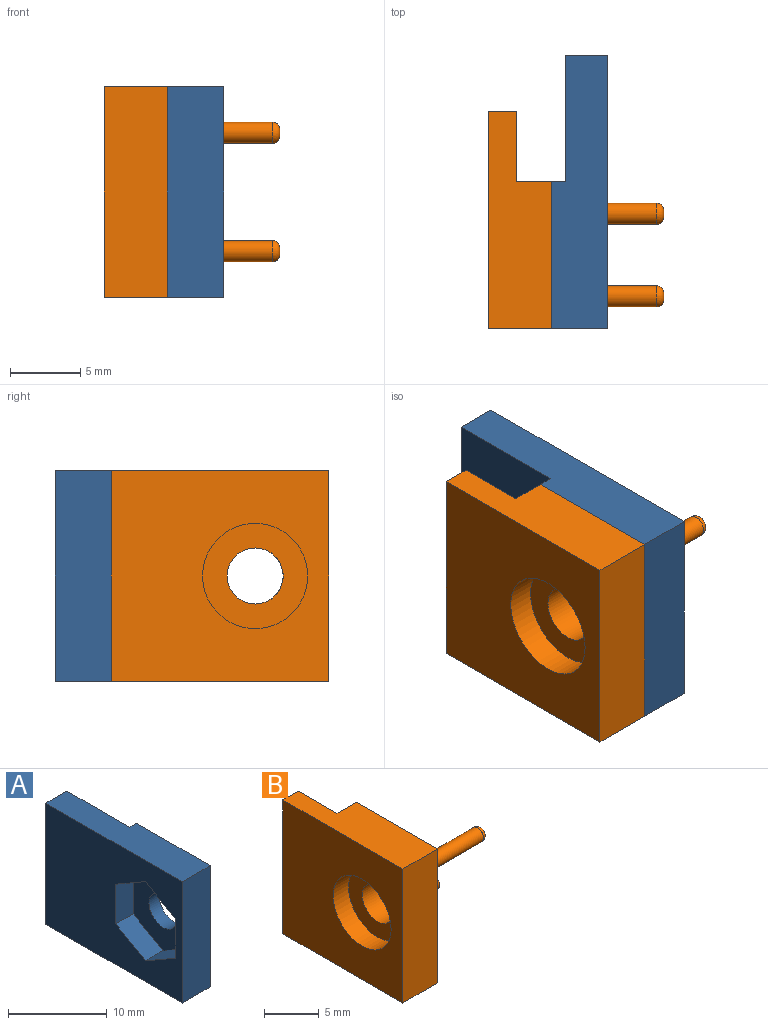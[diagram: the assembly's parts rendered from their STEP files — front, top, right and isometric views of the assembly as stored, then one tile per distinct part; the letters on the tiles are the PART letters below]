
ASSEMBLY  parts=2 mates=1
PART A: 16 faces, bbox 4x19.5x15 mm
  f0: cylinder r=2mm len=4mm, axis (1,0,0), area 18.8mm2, adj f4,f15
  f1: plane 15x3mm, normal (0,1,0), area 45mm2, adj f2,f6,f7,f8
  f2: plane 19.5x15mm, normal (-1,0,0), area 229.9mm2, adj f1,f3,f7,f8,f9,f10,f11,f12
  f3: plane 15x4mm, normal (0,-1,0), area 60mm2, adj f2,f4,f7,f8
  f4: plane 15x10.5mm, normal (1,0,0), area 144.9mm2, adj f0,f3,f5,f7,f8
  f5: plane 15x1mm, normal (0,1,0), area 15mm2, adj f4,f6,f7,f8
  f6: plane 15x9mm, normal (1,0,0), area 135mm2, adj f1,f5,f7,f8
  f7: plane 19.5x4mm, normal (0,0,1), area 69mm2, adj f1,f2,f3,f4,f5,f6
  f8: plane 19.5x4mm, normal (0,0,-1), area 69mm2, adj f1,f2,f3,f4,f5,f6
  f9: plane 4.25x2.5mm, normal (0,0.5,0.87), area 12.3mm2, adj f2,f10,f14,f15
  f10: plane 4.91x2.5mm, normal (0,1,0), area 12.3mm2, adj f2,f9,f11,f15
  f11: plane 4.25x2.5mm, normal (0,0.5,-0.87), area 12.3mm2, adj f2,f10,f12,f15
  f12: plane 4.25x2.5mm, normal (0,-0.5,-0.87), area 12.3mm2, adj f2,f11,f13,f15
  f13: plane 4.91x2.5mm, normal (0,-1,0), area 12.3mm2, adj f2,f12,f14,f15
  f14: plane 4.25x2.5mm, normal (0,-0.5,0.87), area 12.3mm2, adj f2,f9,f13,f15
  f15: plane 9.82x8.5mm, normal (-1,0,0), area 50mm2, adj f0,f9,f10,f11,f12,f13,f14
PART B: 17 faces, bbox 12.5x15.5x15 mm
  f0: cylinder r=2mm len=4mm, axis (1,0,0), area 31.4mm2, adj f4,f9
  f1: plane 15x2mm, normal (0,1,0), area 30mm2, adj f2,f6,f7,f8
  f2: plane 15.5x15mm, normal (-1,0,0), area 188.3mm2, adj f1,f3,f7,f8,f10
  f3: plane 15x4.5mm, normal (0,-1,0), area 67.5mm2, adj f2,f4,f7,f8
  f4: plane 15x10.5mm, normal (1,0,0), area 141.4mm2, adj f0,f3,f5,f7,f8,f11,f13
  f5: plane 15x2.5mm, normal (0,1,0), area 37.5mm2, adj f4,f6,f7,f8
  f6: plane 15x5mm, normal (1,0,0), area 75mm2, adj f1,f5,f7,f8
  f7: plane 15.5x4.5mm, normal (0,0,1), area 57.2mm2, adj f1,f2,f3,f4,f5,f6
  f8: plane 15.5x4.5mm, normal (0,0,-1), area 57.2mm2, adj f1,f2,f3,f4,f5,f6
  f9: plane 7.5x7.5mm, normal (-1,0,0), area 31.6mm2, adj f0,f10
  f10: cylinder r=3.75mm len=7.5mm, axis (-1,0,0), area 47.1mm2, adj f2,f9
  f11: cylinder r=0.75mm len=7.5mm, axis (-1,0,0), area 35.3mm2, adj f4,f16
  f12: plane 0.5x0.5mm, normal (1,0,0), area 0.2mm2, adj f16
  f13: cylinder r=0.75mm len=7.5mm, axis (-1,0,0), area 35.3mm2, adj f4,f15
  f14: plane 0.5x0.5mm, normal (1,0,0), area 0.2mm2, adj f15
  f15: torus R=0.25mm, axis (1,0,0), area 2.8mm2, adj f13,f14
  f16: torus R=0.25mm, axis (1,0,0), area 2.8mm2, adj f11,f12
PLACE A rot(axis=(0,-1,0),180deg) t=(-40.42,0.87,19.18)mm
PLACE B t=(-20.53,0.87,4.18)mm
MATE pin_slot A.f0 <-> B.f0  axis (-1,0,0) through (-30.22,7.35,11.68)mm
